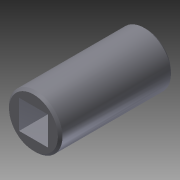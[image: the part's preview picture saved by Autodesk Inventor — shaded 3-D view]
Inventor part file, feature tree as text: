
AUTODESK INVENTOR PART (.ipt)
format: ipt  version: 2014 SP1 (Build 180222100, 222)  size: 102,400 bytes
history: native  units: in
note: dims shown in document units (in); Inventor stores cm internally (conversion verified against a paired STEP export)
features: extrude x2, sketch x2, plane x1, chamfer x1
ambient origin geometry x8: Origin, YZ Plane, XZ Plane, XY Plane, X Axis, Y Axis, Z Axis, Center Point
bodies: Solid1 (feature_tree)
feature tree (6):
  extrude  "Extrusion1"  Depth=0.127in
  plane  "Work Plane1"
  extrude  "Extrusion2"  Depth=0.125in
  chamfer  "Chamfer1"  Distance=0.0635in
  sketch  "Sketch1"  dims[d0=0.2362in d1=0.127in]
  sketch  "Sketch2"  dims[d2=0.127in d3=0.0635in d4=0.0635in d5=0.5in d6=0.0in d7=0.125in d8=0.0in d9=0.01in d10=0.125in d11=45.0deg]
